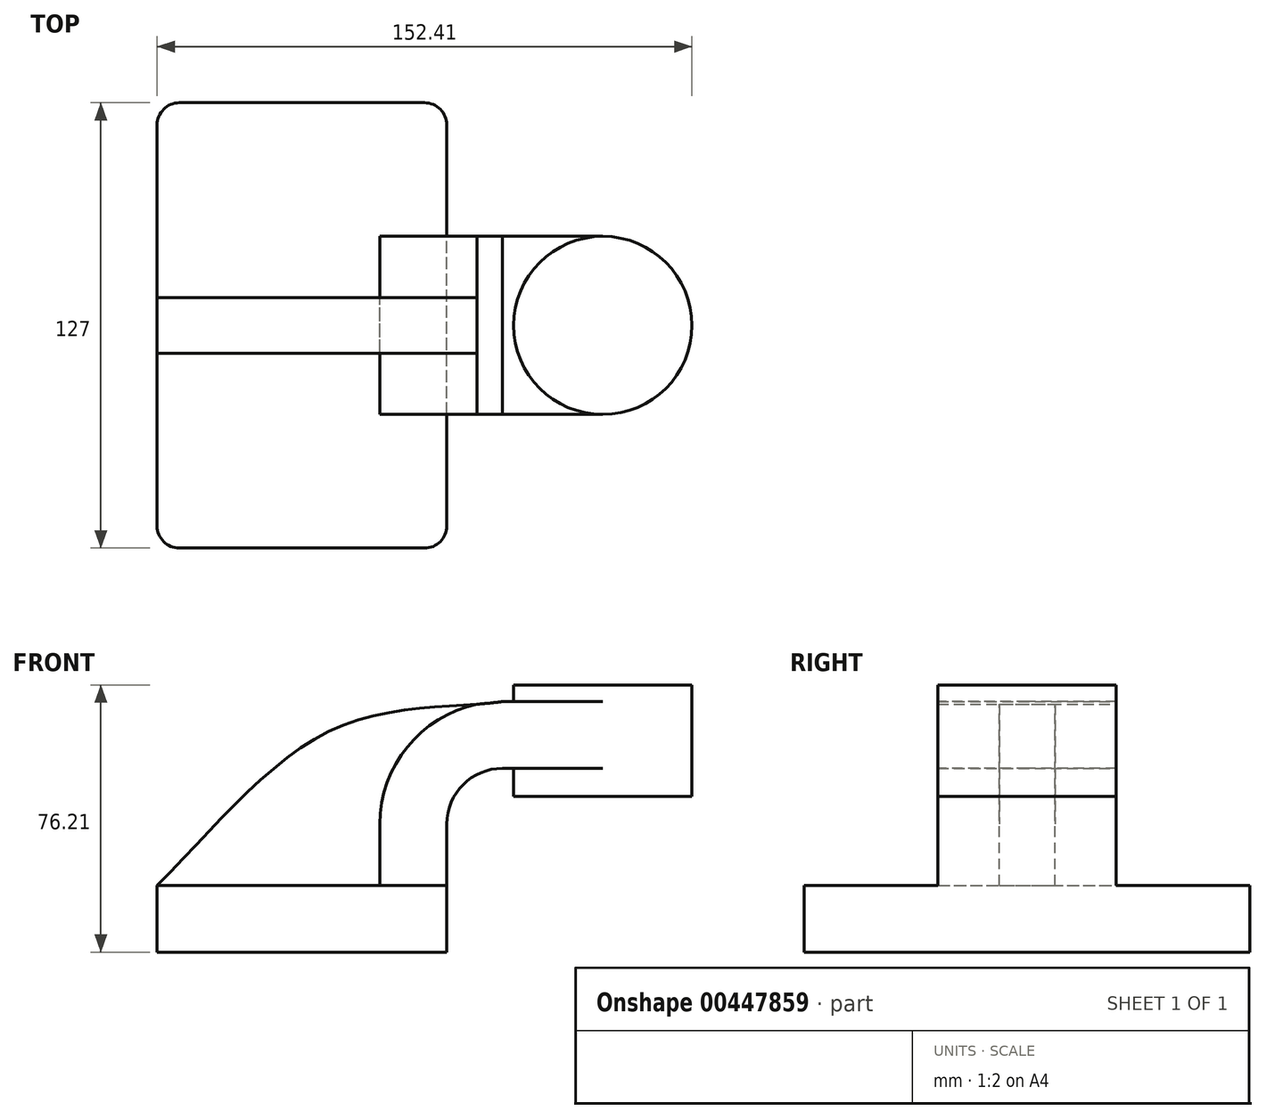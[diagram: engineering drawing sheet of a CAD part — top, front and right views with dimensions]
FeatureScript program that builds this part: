
annotation { "Feature Type Name" : "Feature", "Feature Type Description" : "" }
export const myFeature = defineFeature(function(context is Context, id is Id, definition is map)
    precondition{}
    {
        {
            var Q0;
            Q0=qCreatedBy(makeId("Front.planeOp"),FACE);
            var sketch = newSketch(context, id + "F0", { "sketchPlane" : qUnion([Q0])});
            skLineSegment(sketch, "E0.bottom", {"start": v(-41.28, 9.53) * mm, "end": v(41.28, 9.53) * mm});
            skLineSegment(sketch, "E0.top", {"start": v(-41.28, -9.53) * mm, "end": v(41.28, -9.53) * mm});
            skLineSegment(sketch, "E0.left", {"start": v(-41.28, 9.52) * mm, "end": v(-41.27, -9.53) * mm});
            skLineSegment(sketch, "E0.right", {"start": v(41.28, 9.53) * mm, "end": v(41.28, -9.52) * mm});
            skPoint(sketch, "E0.middle", {"position": v(0, 0) * mm});
            skLineSegment(sketch, "E1.bottom", {"start": v(111.12, 34.93) * mm, "end": v(60.33, 34.93) * mm});
            skLineSegment(sketch, "E1.top", {"start": v(111.12, 66.68) * mm, "end": v(60.33, 66.68) * mm});
            skLineSegment(sketch, "E1.left", {"start": v(111.12, 34.93) * mm, "end": v(111.12, 66.68) * mm});
            skLineSegment(sketch, "E1.right", {"start": v(60.33, 34.93) * mm, "end": v(60.33, 66.68) * mm});
            skPoint(sketch, "E1.middle", {"position": v(85.72, 50.8) * mm});
            skLineSegment(sketch, "E2", {"start": v(41.27, 9.53) * mm, "end": v(41.27, 27) * mm});
            skArc(sketch, "E3", {"start": v(41.27, 27) * mm, "mid": v(45.92, 38.23) * mm, "end": v(57.15, 42.88) * mm});
            skLineSegment(sketch, "E4", {"start": v(57.15, 42.88) * mm, "end": v(85.72, 42.88) * mm});
            skPoint(sketch, "E4.endSnap0", {"position": v(85.72, 34.93) * mm});
            skLineSegment(sketch, "E5.0", {"start": v(57.15, 61.93) * mm, "end": v(85.72, 61.93) * mm});
            skArc(sketch, "E5.1", {"start": v(22.22, 27) * mm, "mid": v(32.45, 51.7) * mm, "end": v(57.15, 61.93) * mm});
            skLineSegment(sketch, "E5.2", {"start": v(22.23, 9.53) * mm, "end": v(22.23, 27) * mm});
            skLineSegment(sketch, "E6", {"start": v(85.72, 34.93) * mm, "end": v(85.72, 66.68) * mm});
            skFitSpline(sketch, "E7", {"points": [v(-41.28, 9.52) * mm, v(10.56, 54.7) * mm, v(57.15, 61.93) * mm], "startDerivative": vector(94.43, 94.8) * mm, "endDerivative": vector(81.9, 12.29) * mm});
            skSolve(sketch);
        }
        {
            var Q0;
            Q0=makeQuery(id+"F0.imprint","IMPRINT",FACE,{"disambiguationData":[TD([[makeQuery(id+"F0.imprint","IMPRINT",EDGE,{"derivedFrom":sQuery(id+"F0.wireOp",EDGE,"E0.top")}),1.0]])]});
            extrude(context, id + "F1", {"entities" : qUnion([Q0]), "depth" : 127 * mm, "symmetric" : true});
        }
        {
            var Q0;
            {var subQ1=sQuery(id+"F0.wireOp",EDGE,"E2");Q0=makeQuery(id+"F0.imprint","IMPRINT",FACE,{"disambiguationData":[TD([[makeQuery(id+"F0.imprint","IMPRINT",EDGE,{"derivedFrom":subQ1}),1.0]])]});}
            var Q1;
            {var subQ0=sQuery(id+"F0.wireOp",EDGE,"E4");var subQ1=sQuery(id+"F0.wireOp",EDGE,"E1.right");var subQ2=makeQuery(id+"F0.imprint","INTERSECT",VERTEX,{"derivedFrom":[subQ1,subQ0]});Q1=makeQuery(id+"F0.imprint","IMPRINT",FACE,{"disambiguationData":[TD([[makeQuery(id+"F0.imprint","IMPRINT",EDGE,{"disambiguationData":[TD([[subQ2,-1.0]])],"derivedFrom":subQ1}),-1.0]])]});}
            extrude(context, id + "F2", {"entities" : qUnion([Q0, Q1]), "operationType" : NewBodyOperationType.ADD, "depth" : 50.8 * mm, "symmetric" : true});
        }
        {
            var Q0;
            {var subQ3=sQuery(id+"F0.wireOp",EDGE,"E5.2");Q0=makeQuery(id+"F0.imprint","IMPRINT",FACE,{"disambiguationData":[TD([[makeQuery(id+"F0.imprint","IMPRINT",EDGE,{"derivedFrom":subQ3}),1.0]])]});}
            extrude(context, id + "F3", {"entities" : qUnion([Q0]), "depth" : 15.88 * mm, "symmetric" : true});
        }
        {
            var Q0;
            {var subQ0=sQuery(id+"F0.wireOp",EDGE,"E1.left");Q0=makeQuery(id+"F0.imprint","IMPRINT",FACE,{"disambiguationData":[TD([[makeQuery(id+"F0.imprint","IMPRINT",EDGE,{"derivedFrom":subQ0}),1.0]])]});}
            var Q1;
            Q1=sQuery(id+"F0.wireOp",EDGE,"E6");
            revolve(context, id + "F4", {"operationType" : NewBodyOperationType.ADD, "entities" : qUnion([Q0]), "axis" : qUnion([Q1]), "revolveType" : RevolveType.FULL});
        }
        {
            var Q0;
            Q0=makeQuery(id+"F1.opExtrude","CAP_EDGE",EDGE,{"disambiguationData":[OSD([sQuery(id+"F0.wireOp",EDGE,"E0.left")])],"isStart":false});
            var Q1;
            Q1=makeQuery(id+"F1.opExtrude","CAP_EDGE",EDGE,{"disambiguationData":[OSD([sQuery(id+"F0.wireOp",EDGE,"E0.right")])],"isStart":false});
            var Q2;
            Q2=makeQuery(id+"F1.opExtrude","CAP_EDGE",EDGE,{"disambiguationData":[OSD([sQuery(id+"F0.wireOp",EDGE,"E0.right")])],"isStart":true});
            var Q3;
            Q3=makeQuery(id+"F1.opExtrude","CAP_EDGE",EDGE,{"disambiguationData":[OSD([sQuery(id+"F0.wireOp",EDGE,"E0.left")])],"isStart":true});
            fillet(context, id + "F5", {"entities" : qUnion([Q0, Q1, Q2, Q3]), "radius" : 6.35 * mm, "tangentPropagation" : true, "allowEdgeOverflow" : false});
        }
    });
